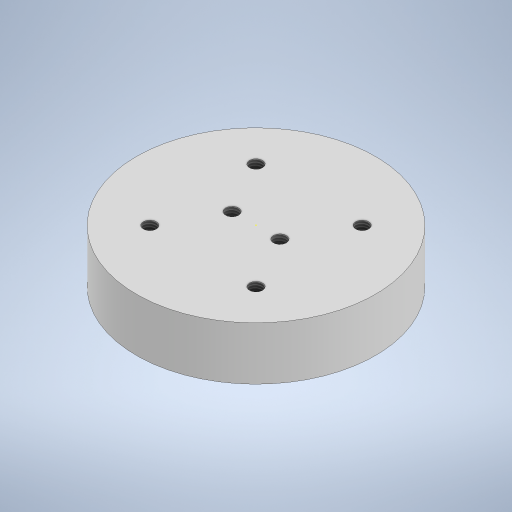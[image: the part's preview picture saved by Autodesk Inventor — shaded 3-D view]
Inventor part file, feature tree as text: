
AUTODESK INVENTOR PART (.ipt)
format: ipt  version: 2023 (Build 270158000, 158)  size: 239,104 bytes
history: native  units: mm
features: sketch x4, hole x2, other x1, extrude x1
ambient origin geometry x8: Origin, YZ Plane, XZ Plane, XY Plane, X Axis, Y Axis, Z Axis, Center Point
bodies: Body1 (feature_tree)
feature tree (8):
  other  "Твердое тело1"
  extrude  "Выдавливание1"  Depth=45.0mm
  hole  "Отверстие1"  [1 undecoded]
  sketch  "Эскиз3"
  hole  "Отверстие2"  [1 undecoded]
  sketch  "Эскиз1"
  sketch  "Эскиз2"
  sketch  "Эскиз4"
note: 2 required parameter values undecoded (feature->parameter linkage not recoverable at this tier; creation-order binding heuristic only, values carry confidence <= 0.55)
